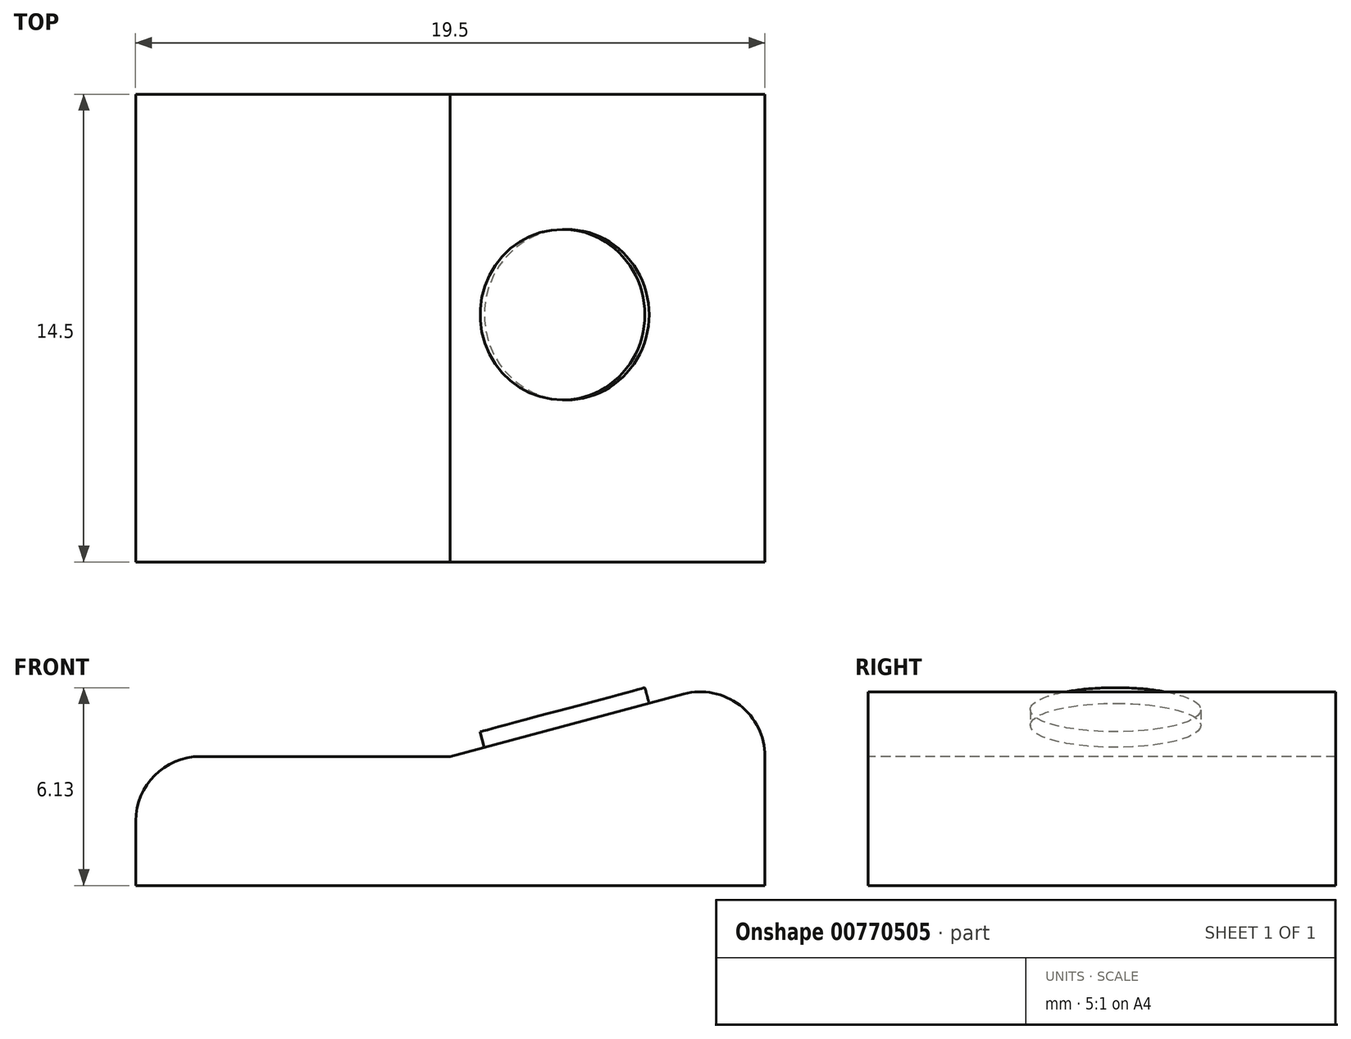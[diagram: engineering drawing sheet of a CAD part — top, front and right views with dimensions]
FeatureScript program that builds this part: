
annotation { "Feature Type Name" : "Feature", "Feature Type Description" : "" }
export const myFeature = defineFeature(function(context is Context, id is Id, definition is map)
    precondition{}
    {
        {
            var Q0;
            Q0=qCreatedBy(makeId("Top.planeOp"),FACE);
            var sketch = newSketch(context, id + "F0", { "sketchPlane" : qUnion([Q0])});
            skLineSegment(sketch, "E0.bottom", {"start": v(-12.82, 6.83) * mm, "end": v(6.68, 6.83) * mm});
            skLineSegment(sketch, "E0.top", {"start": v(-12.82, -7.67) * mm, "end": v(6.68, -7.67) * mm});
            skLineSegment(sketch, "E0.left", {"start": v(-12.82, 6.83) * mm, "end": v(-12.82, -7.67) * mm});
            skLineSegment(sketch, "E0.right", {"start": v(6.68, 6.83) * mm, "end": v(6.68, -7.67) * mm});
            skSolve(sketch);
        }
        {
            var Q0;
            Q0=makeQuery(id+"F0.imprint","IMPRINT",FACE,{"disambiguationData":[TD([[makeQuery(id+"F0.imprint","IMPRINT",EDGE,{"derivedFrom":sQuery(id+"F0.wireOp",EDGE,"E0.bottom")}),-1.0]])]});
            extrude(context, id + "F1", {"entities" : qUnion([Q0]), "depth" : 4 * mm, "offsetDistance" : 25 * mm});
        }
        {
            var Q0;
            Q0=makeQuery(id+"F1.opExtrude","SWEPT_FACE",FACE,{"disambiguationData":[OSD([sQuery(id+"F0.wireOp",EDGE,"E0.top")])]});
            var sketch = newSketch(context, id + "F2", { "sketchPlane" : qUnion([Q0])});
            skLineSegment(sketch, "E1", {"start": v(6.68, 4) * mm, "end": v(6.68, 6.61) * mm});
            skLineSegment(sketch, "E2", {"start": v(6.68, 6.61) * mm, "end": v(-3.07, 4) * mm});
            skLineSegment(sketch, "E3", {"start": v(-3.07, 4) * mm, "end": v(6.68, 4) * mm});
            skSolve(sketch);
        }
        {
            var Q0;
            Q0=makeQuery(id+"F2.imprint","IMPRINT",FACE,{"disambiguationData":[TD([[makeQuery(id+"F2.imprint","IMPRINT",EDGE,{"derivedFrom":sQuery(id+"F2.wireOp",EDGE,"E1")}),1.0]])]});
            extrude(context, id + "F3", {"entities" : qUnion([Q0]), "operationType" : NewBodyOperationType.ADD, "oppositeDirection" : true, "depth" : 14.5 * mm, "offsetDistance" : 25 * mm});
        }
        {
            var Q0;
            Q0=makeQuery(id+"F3.opExtrude","SWEPT_EDGE",EDGE,{"disambiguationData":[OSD([sQuery(id+"F0.wireOp",EDGE,"E0.top"),sQuery(id+"F2.wireOp",EDGE,"E2"),sQuery(id+"F2.wireOp",EDGE,"E3")])]});
            var Q1;
            Q1=makeQuery(id+"F3.opExtrude","SWEPT_EDGE",EDGE,{"disambiguationData":[OSD([sQuery(id+"F2.wireOp",EDGE,"E1"),sQuery(id+"F2.wireOp",EDGE,"E2")])]});
            var Q2;
            Q2=makeQuery(id+"F1.opExtrude","CAP_EDGE",EDGE,{"disambiguationData":[OSD([sQuery(id+"F0.wireOp",EDGE,"E0.left")])],"isStart":false});
            fillet(context, id + "F4", {"entities" : qUnion([Q0, Q1, Q2]), "radius" : 2 * mm, "tangentPropagation" : true, "allowEdgeOverflow" : false});
        }
        {
            var Q0;
            Q0=makeQuery(id+"F3.opExtrude","SWEPT_FACE",FACE,{"disambiguationData":[OSD([sQuery(id+"F2.wireOp",EDGE,"E2")])]});
            var sketch = newSketch(context, id + "F5", { "sketchPlane" : qUnion([Q0])});
            skCircle(sketch, "E4", {"center": v(1.8, 0) * mm, "radius": 2.64 * mm});
            skSolve(sketch);
        }
        {
            var Q0;
            Q0 = qSketchRegion(id + "F5", true);
            extrude(context, id + "F6", {"entities" : qUnion([Q0]), "depth" : 0.5 * mm, "offsetDistance" : 25 * mm});
        }
    });
